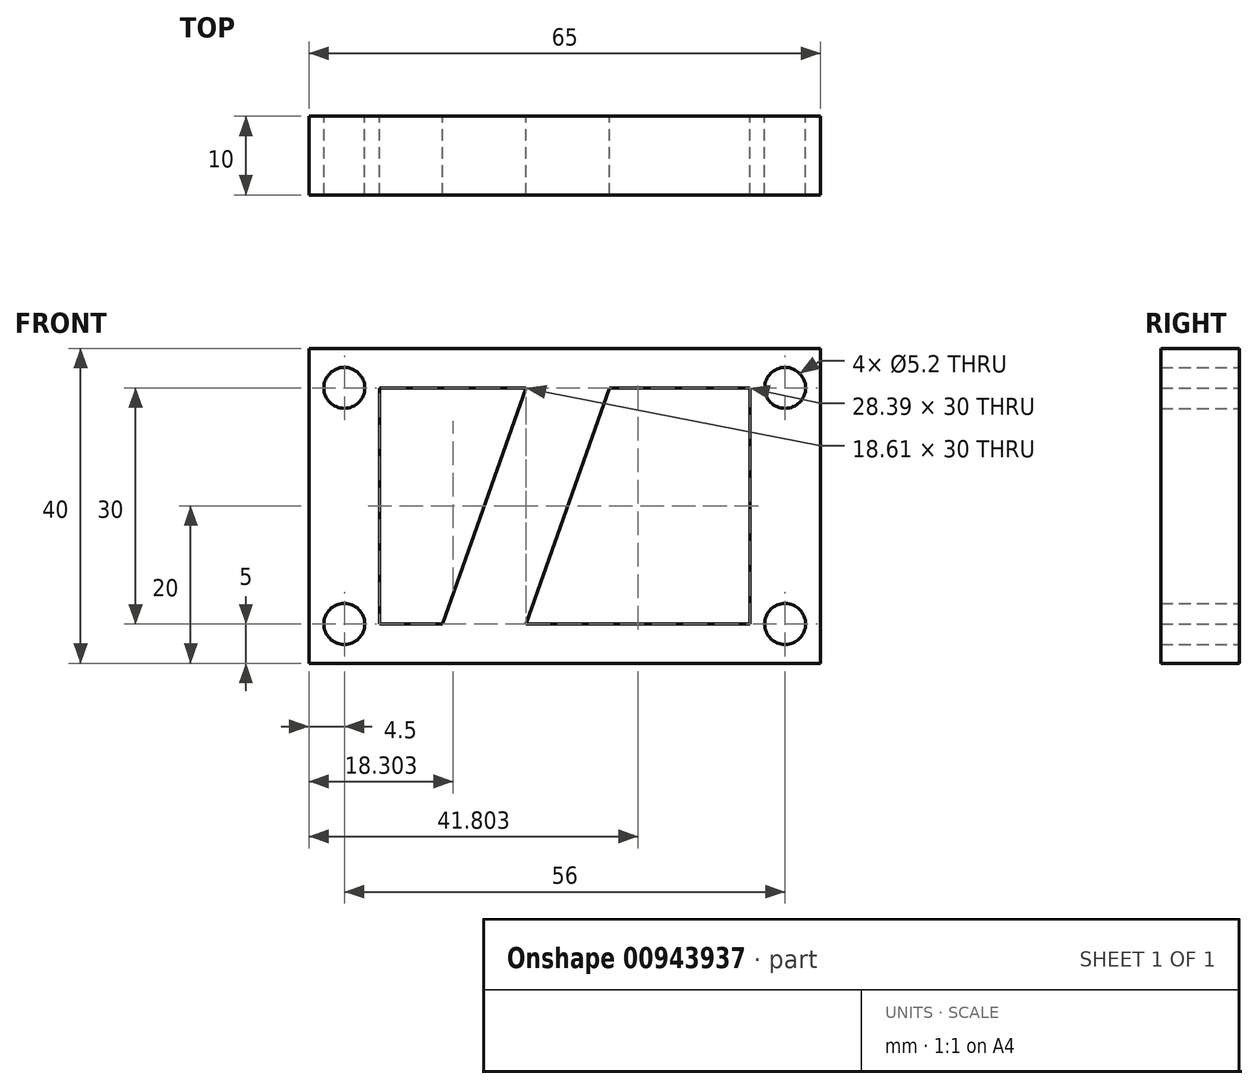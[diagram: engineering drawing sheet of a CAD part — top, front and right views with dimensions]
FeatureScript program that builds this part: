
annotation { "Feature Type Name" : "Feature", "Feature Type Description" : "" }
export const myFeature = defineFeature(function(context is Context, id is Id, definition is map)
    precondition{}
    {
        {
            var Q0;
            Q0=qCreatedBy(makeId("Front.planeOp"),FACE);
            var sketch = newSketch(context, id + "F0", { "sketchPlane" : qUnion([Q0])});
            skLineSegment(sketch, "E0.bottom", {"start": v(32.5, 20) * mm, "end": v(-32.5, 20) * mm});
            skLineSegment(sketch, "E0.top", {"start": v(32.5, -20) * mm, "end": v(-32.5, -20) * mm});
            skLineSegment(sketch, "E0.left", {"start": v(32.5, 20) * mm, "end": v(32.5, -20) * mm});
            skLineSegment(sketch, "E0.right", {"start": v(-32.5, 20) * mm, "end": v(-32.5, -20) * mm});
            skPoint(sketch, "E0.middle", {"position": v(0, 0) * mm});
            skCircle(sketch, "E1", {"center": v(-28, 15) * mm, "radius": 2.6 * mm});
            skCircle(sketch, "E2", {"center": v(-28, -15) * mm, "radius": 2.6 * mm});
            skCircle(sketch, "E3", {"center": v(28, 15) * mm, "radius": 2.6 * mm});
            skCircle(sketch, "E4", {"center": v(28, -15) * mm, "radius": 2.6 * mm});
            skLineSegment(sketch, "E5", {"start": v(-28, 15) * mm, "end": v(-28, -15) * mm, "construction": true});
            skLineSegment(sketch, "E6", {"start": v(28, 15) * mm, "end": v(28, -15) * mm, "construction": true});
            skLineSegment(sketch, "E7", {"start": v(-28, 15) * mm, "end": v(28, -15) * mm, "construction": true});
            skLineSegment(sketch, "E8", {"start": v(-28, 15) * mm, "end": v(28, 15) * mm, "construction": true});
            skLineSegment(sketch, "E9", {"start": v(-23.5, 15) * mm, "end": v(-4.9, 15) * mm});
            skLineSegment(sketch, "E10", {"start": v(-4.9, 15) * mm, "end": v(-15.5, -15) * mm});
            skLineSegment(sketch, "E11", {"start": v(-15.5, -15) * mm, "end": v(-23.5, -15) * mm});
            skLineSegment(sketch, "E12", {"start": v(-23.5, -15) * mm, "end": v(-23.5, 15) * mm});
            skLineSegment(sketch, "E13", {"start": v(-4.9, -15) * mm, "end": v(5.71, 15) * mm});
            skLineSegment(sketch, "E14", {"start": v(5.71, 15) * mm, "end": v(23.5, 15) * mm});
            skLineSegment(sketch, "E15", {"start": v(23.5, 15) * mm, "end": v(23.5, -15) * mm});
            skLineSegment(sketch, "E16", {"start": v(23.5, -15) * mm, "end": v(-4.9, -15) * mm});
            skSolve(sketch);
        }
        {
            var Q0;
            Q0 = qSketchRegion(id + "F0", true);
            extrude(context, id + "F1", {"entities" : qUnion([Q0]), "depth" : 5 * mm, "offsetDistance" : 25 * mm, "hasSecondDirection" : true, "secondDirectionOppositeDirection" : true, "secondDirectionDepth" : 5 * mm});
        }
    });
